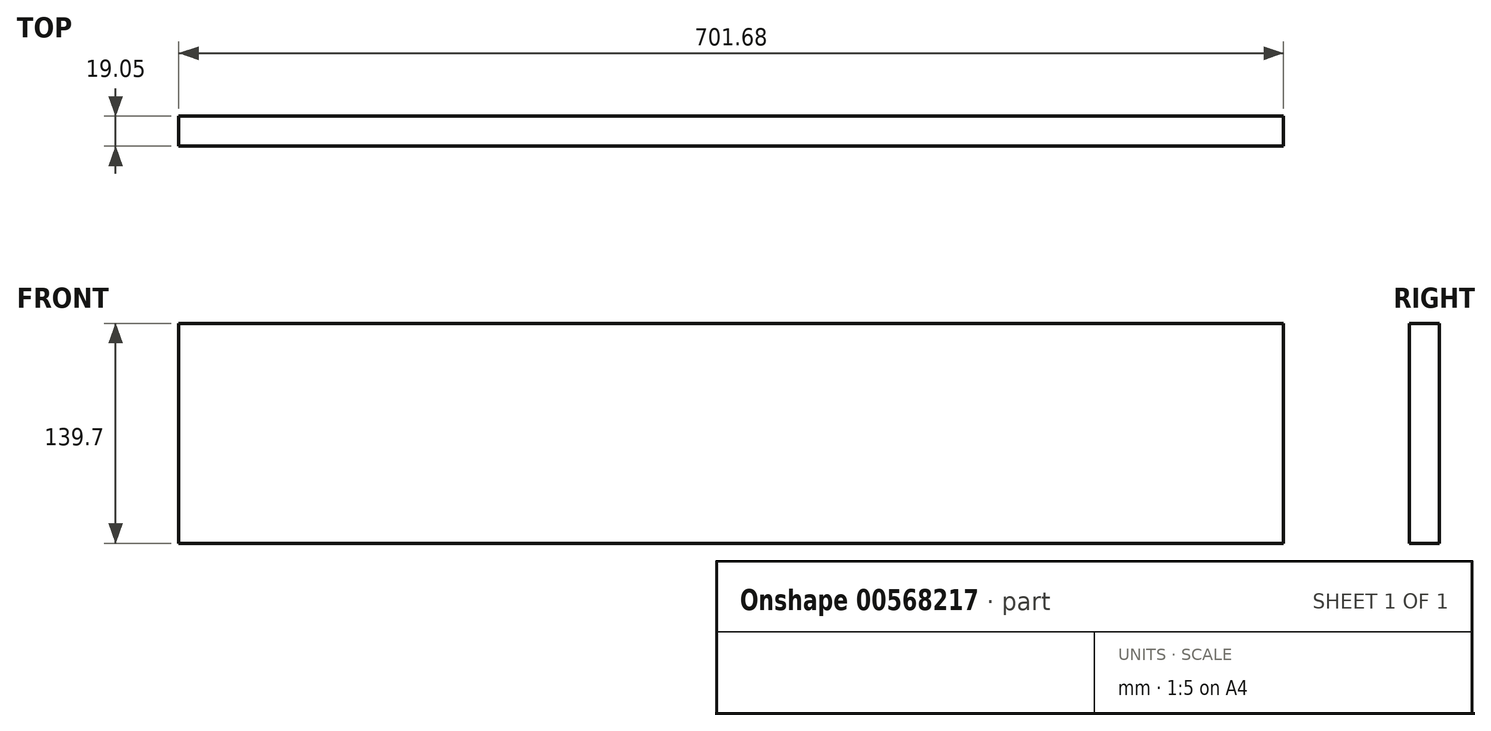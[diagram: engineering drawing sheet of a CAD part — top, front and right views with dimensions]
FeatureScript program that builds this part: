
annotation { "Feature Type Name" : "Feature", "Feature Type Description" : "" }
export const myFeature = defineFeature(function(context is Context, id is Id, definition is map)
    precondition{}
    {
        {
            var Q0;
            Q0=qCreatedBy(makeId("Front.planeOp"),FACE);
            var sketch = newSketch(context, id + "F0", { "sketchPlane" : qUnion([Q0])});
            skLineSegment(sketch, "E0.bottom", {"start": v(0, 0) * mm, "end": v(701.68, 0) * mm});
            skLineSegment(sketch, "E0.top", {"start": v(0, 139.7) * mm, "end": v(701.68, 139.7) * mm});
            skLineSegment(sketch, "E0.left", {"start": v(0, 0) * mm, "end": v(0, 139.7) * mm});
            skLineSegment(sketch, "E0.right", {"start": v(701.68, 0) * mm, "end": v(701.68, 139.7) * mm});
            skSolve(sketch);
        }
        {
            var Q0;
            Q0=makeQuery(id+"F0.imprint","IMPRINT",FACE,{"disambiguationData":[TD([[makeQuery(id+"F0.imprint","IMPRINT",EDGE,{"derivedFrom":sQuery(id+"F0.wireOp",EDGE,"E0.bottom")}),1.0]])]});
            extrude(context, id + "F1", {"entities" : qUnion([Q0]), "depth" : 19.05 * mm, "offsetDistance" : 25.4 * mm});
        }
    });
